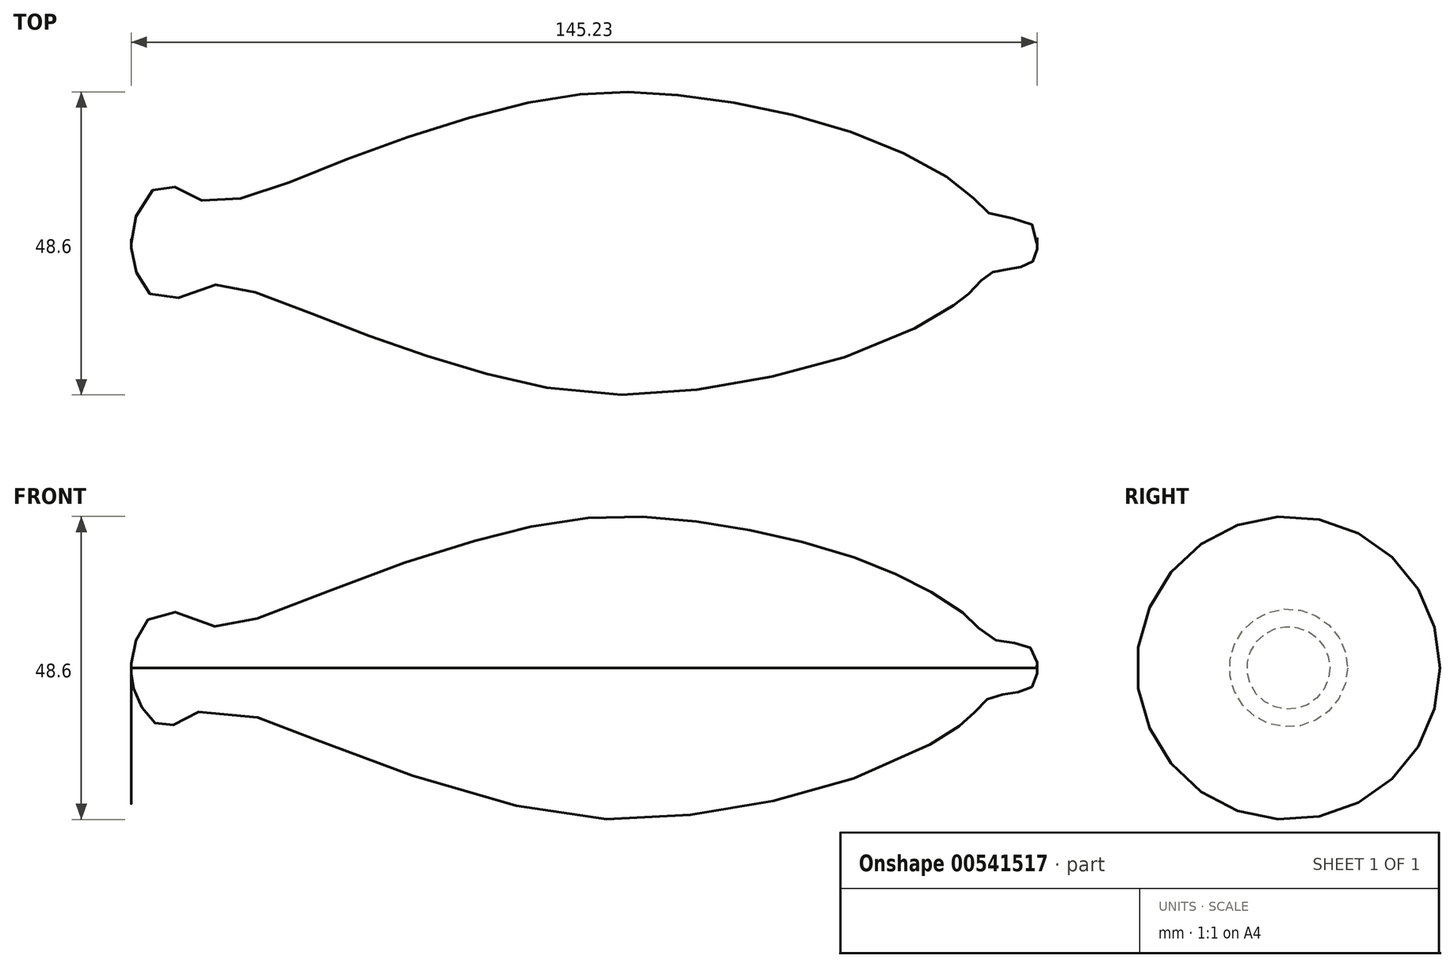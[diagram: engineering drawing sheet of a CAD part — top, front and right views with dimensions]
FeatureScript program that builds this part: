
annotation { "Feature Type Name" : "Feature", "Feature Type Description" : "" }
export const myFeature = defineFeature(function(context is Context, id is Id, definition is map)
    precondition{}
    {
        {
            var Q0;
            Q0=qCreatedBy(makeId("Top.planeOp"),FACE);
            var sketch = newSketch(context, id + "F0", { "sketchPlane" : qUnion([Q0])});
            skFitSpline(sketch, "E0", {"points": [v(-76.47, 6.88) * mm, v(-82.76, 9.44) * mm, v(-87.28, 3.93) * mm, v(-87.28, -2.56) * mm, v(-83.35, -7.47) * mm, v(-76.27, -4.52) * mm, v(-60.94, -6.1) * mm, v(-30.47, -17.89) * mm, v(0, -22.8) * mm, v(26.15, -20.44) * mm, v(45.02, -8.65) * mm, v(48.56, -4.91) * mm, v(51.7, -3.74) * mm, v(56.22, -2.16) * mm, v(57.2, 1.97) * mm, v(55.04, 3.74) * mm, v(49.93, 4.72) * mm, v(46.79, 7.67) * mm, v(30.27, 16.9) * mm, v(0, 23.79) * mm, v(-22.02, 23) * mm, v(-55.63, 12.58) * mm, v(-76.47, 6.88) * mm]});
            skLineSegment(sketch, "E1", {"start": v(57.27, 0) * mm, "end": v(-87.85, 0) * mm});
            skSolve(sketch);
        }
        {
            var Q0;
            {var subQ0=sQuery(id+"F0.wireOp",EDGE,"E1");Q0=makeQuery(id+"F0.imprint","IMPRINT",FACE,{"disambiguationData":[TD([[makeQuery(id+"F0.imprint","IMPRINT",EDGE,{"derivedFrom":subQ0}),-1.0]])]});}
            var Q1;
            Q1=sQuery(id+"F0.wireOp",EDGE,"E1");
            revolve(context, id + "F1", {"entities" : qUnion([Q0]), "axis" : qUnion([Q1]), "revolveType" : RevolveType.FULL});
        }
    });
